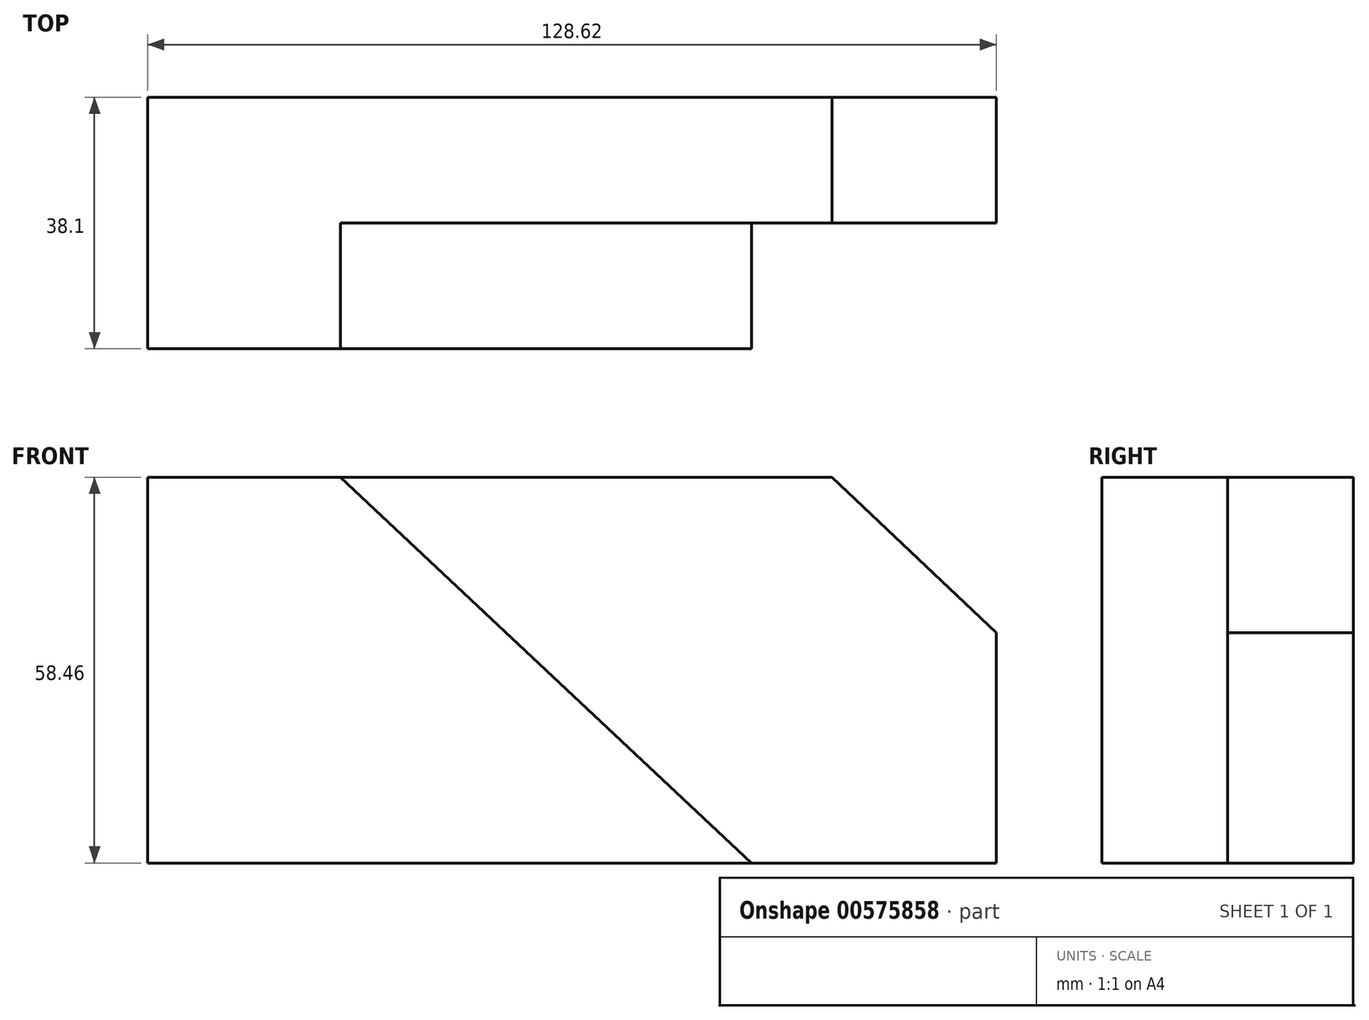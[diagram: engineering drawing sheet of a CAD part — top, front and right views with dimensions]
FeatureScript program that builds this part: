
annotation { "Feature Type Name" : "Feature", "Feature Type Description" : "" }
export const myFeature = defineFeature(function(context is Context, id is Id, definition is map)
    precondition{}
    {
        {
            var Q0;
            Q0=qCreatedBy(makeId("Front.planeOp"),FACE);
            var sketch = newSketch(context, id + "F0", { "sketchPlane" : qUnion([Q0])});
            skLineSegment(sketch, "E0", {"start": v(-64.44, 23.55) * mm, "end": v(-64.44, -34.91) * mm});
            skLineSegment(sketch, "E1", {"start": v(-64.44, -34.91) * mm, "end": v(64.18, -34.91) * mm});
            skLineSegment(sketch, "E2", {"start": v(-64.44, 23.55) * mm, "end": v(39.32, 23.55) * mm});
            skPoint(sketch, "E3.end.orphan", {"position": v(64.18, 0) * mm});
            skLineSegment(sketch, "E4", {"start": v(64.18, 0) * mm, "end": v(64.18, -34.91) * mm});
            skLineSegment(sketch, "E5", {"start": v(39.32, 23.55) * mm, "end": v(64.18, 0) * mm});
            skPoint(sketch, "E6.start.orphan", {"position": v(64.18, 33.23) * mm});
            skPoint(sketch, "E7.orphan", {"position": v(64.18, 23.55) * mm});
            skLineSegment(sketch, "E8", {"start": v(-35.21, 23.55) * mm, "end": v(27.11, -34.91) * mm});
            skPoint(sketch, "E9.start.orphan", {"position": v(-64.44, 27.14) * mm});
            skSolve(sketch);
        }
        {
            var Q0;
            {var subQ0=sQuery(id+"F0.wireOp",EDGE,"E0");Q0=makeQuery(id+"F0.imprint","IMPRINT",FACE,{"disambiguationData":[TD([[makeQuery(id+"F0.imprint","IMPRINT",EDGE,{"derivedFrom":subQ0}),1.0]])]});}
            extrude(context, id + "F1", {"entities" : qUnion([Q0]), "depth" : 38.1 * mm, "offsetDistance" : 25.4 * mm});
        }
        {
            var Q0;
            {var subQ1=sQuery(id+"F0.wireOp",EDGE,"E4");Q0=makeQuery(id+"F0.imprint","IMPRINT",FACE,{"disambiguationData":[TD([[makeQuery(id+"F0.imprint","IMPRINT",EDGE,{"derivedFrom":subQ1}),-1.0]])]});}
            extrude(context, id + "F2", {"entities" : qUnion([Q0]), "operationType" : NewBodyOperationType.ADD, "depth" : 19.05 * mm, "offsetDistance" : 25.4 * mm});
        }
    });
